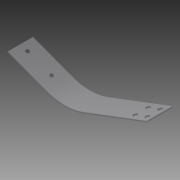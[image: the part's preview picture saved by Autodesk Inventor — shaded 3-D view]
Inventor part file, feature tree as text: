
AUTODESK INVENTOR PART (.ipt)
format: ipt  version: 2014 SP1 (Build 180222100, 222)  size: 155,136 bytes
history: native  units: in
note: dims shown in document units (in); Inventor stores cm internally (conversion verified against a paired STEP export)
features: sketch x5, extrude x4, other x1, fillet x1
ambient origin geometry x8: Origin, YZ Plane, XZ Plane, XY Plane, X Axis, Y Axis, Z Axis, Center Point
bodies: Solid1 (feature_tree)
feature tree (11):
  extrude  "Extrusion1"  Depth=1.0in
  extrude  "Extrusion2"  Depth=0.0625in
  other  "Bend Part1"
  extrude  "Extrusion3"  Depth=0.25in
  extrude  "Extrusion4"  Depth=0.0625in TaperAngle=0.0deg
  fillet  "Fillet1"  Radius=3.4in
  sketch  "Sketch1"  dims[d0=7.0in d1=1.0in]
  sketch  "Sketch2"  dims[d2=0.0625in d3=0.0in d6=0.15in]
  sketch  "Sketch3"  dims[d7=0.25in d8=0.25in]
  sketch  "Sketch4"  dims[d9=0.7874in d11=0.5in d12=0.7874in d14=0.5in d17=0.0625in d18=0.0in d20=3.4in]
  sketch  "Sketch5"  dims[d21=2.0in d22=0.285in d23=1.25in d24=0.0625in d25=0.0in d26=0.15in d27=0.302in d28=0.5in d29=0.7874in d31=1.0in d32=0.3937in d34=1.0in d36=0.0625in d37=0.0in d38=0.02in]
